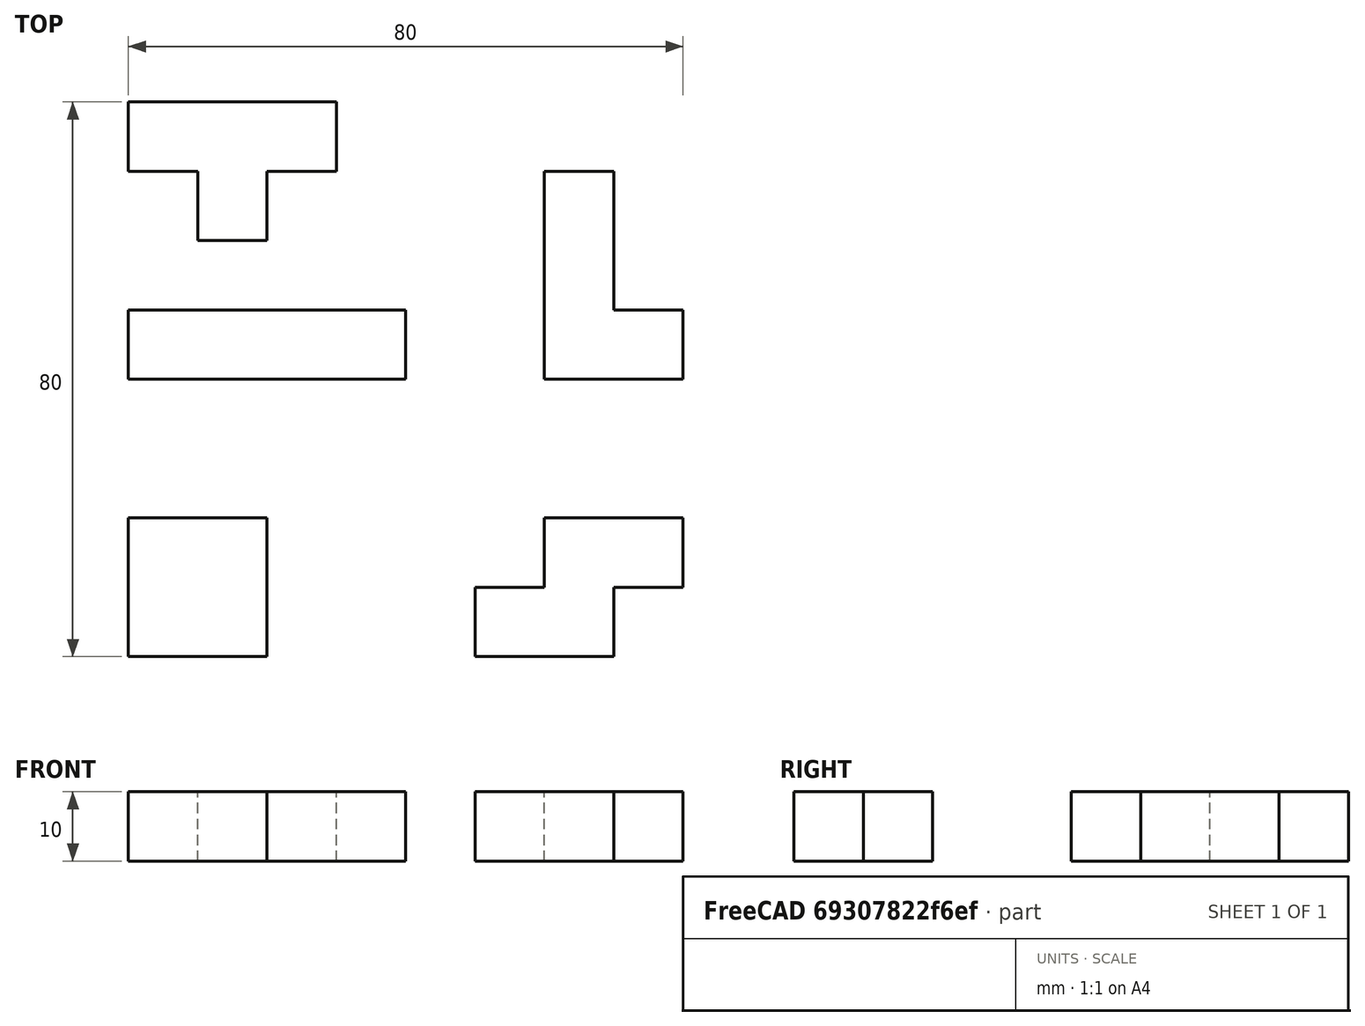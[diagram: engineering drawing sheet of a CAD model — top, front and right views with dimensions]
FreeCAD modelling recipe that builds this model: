
FCSTD DOCUMENT  (FreeCAD 1.0R39319 (Git))
Label: ojt1_t05r03_tetris
License: All rights reserved
LicenseURL: https://en.wikipedia.org/wiki/All_rights_reserved
objects: Part::Box×13, Part::MultiFuse×4
note: 17 computed .brp shape members not serialized (recipe doc carries the construction recipe); baked Part::Feature solids carry a one-line shape summary decoded from their .brp

FEATURE [Part::Box] Box  label="Cub"
  AttacherType = Attacher::AttachEngine3D
  Height = 10
  Length = 40
  Width = 10
FEATURE [Part::Box] Box001  label="Cub001"
  AttacherType = Attacher::AttachEngine3D
  Height = 10
  Length = 30
  Placement = pos=(0,30,0) rot=(0,0,1;0rad)
  Width = 10
FEATURE [Part::Box] Box002  label="Cub002"
  AttacherType = Attacher::AttachEngine3D
  Height = 10
  Length = 10
  Placement = pos=(10,20,0) rot=(0,0,1;0rad)
  Width = 10
FEATURE [Part::MultiFuse] Fusion
  Refine = true
  Shapes = -> [Box002,Box001]
FEATURE [Part::Box] Box003  label="Cub003"
  AttacherType = Attacher::AttachEngine3D
  Height = 10
  Length = 10
  Placement = pos=(0,-30,0) rot=(0,0,1;0rad)
  Width = 10
FEATURE [Part::Box] Box004  label="Cub004"
  AttacherType = Attacher::AttachEngine3D
  Height = 10
  Length = 10
  Placement = pos=(10,-30,0) rot=(0,0,1;0rad)
  Width = 10
FEATURE [Part::Box] Box005  label="Cub005"
  AttacherType = Attacher::AttachEngine3D
  Height = 10
  Length = 10
  Placement = pos=(0,-40,0) rot=(0,0,1;0rad)
  Width = 10
FEATURE [Part::Box] Box006  label="Cub006"
  AttacherType = Attacher::AttachEngine3D
  Height = 10
  Length = 10
  Placement = pos=(10,-40,0) rot=(0,0,1;0rad)
  Width = 10
FEATURE [Part::MultiFuse] Fusion001
  Refine = true
  Shapes = -> [Box006,Box003,Box004,Box005]
FEATURE [Part::Box] Box007  label="Cub007"
  AttacherType = Attacher::AttachEngine3D
  Height = 10
  Length = 30
  Placement = pos=(70,0,0) rot=(0,0,1;1.5708rad)
  Width = 10
FEATURE [Part::Box] Box008  label="Cub008"
  AttacherType = Attacher::AttachEngine3D
  Height = 10
  Length = 10
  Placement = pos=(70,0,0) rot=(0,0,1;0rad)
  Width = 10
FEATURE [Part::MultiFuse] Fusion002
  Refine = true
  Shapes = -> [Box008,Box007]
FEATURE [Part::Box] Box009  label="Cub009"
  AttacherType = Attacher::AttachEngine3D
  Height = 10
  Length = 10
  Placement = pos=(50,-40,0) rot=(0,0,1;0rad)
  Width = 10
FEATURE [Part::Box] Box010  label="Cub010"
  AttacherType = Attacher::AttachEngine3D
  Height = 10
  Length = 10
  Placement = pos=(60,-40,0) rot=(0,0,1;0rad)
  Width = 10
FEATURE [Part::Box] Box011  label="Cub011"
  AttacherType = Attacher::AttachEngine3D
  Height = 10
  Length = 10
  Placement = pos=(60,-30,0) rot=(0,0,1;0rad)
  Width = 10
FEATURE [Part::Box] Box012  label="Cub012"
  AttacherType = Attacher::AttachEngine3D
  Height = 10
  Length = 10
  Placement = pos=(70,-30,0) rot=(0,0,1;0rad)
  Width = 10
FEATURE [Part::MultiFuse] Fusion003
  Refine = true
  Shapes = -> [Box012,Box009,Box010,Box011]
